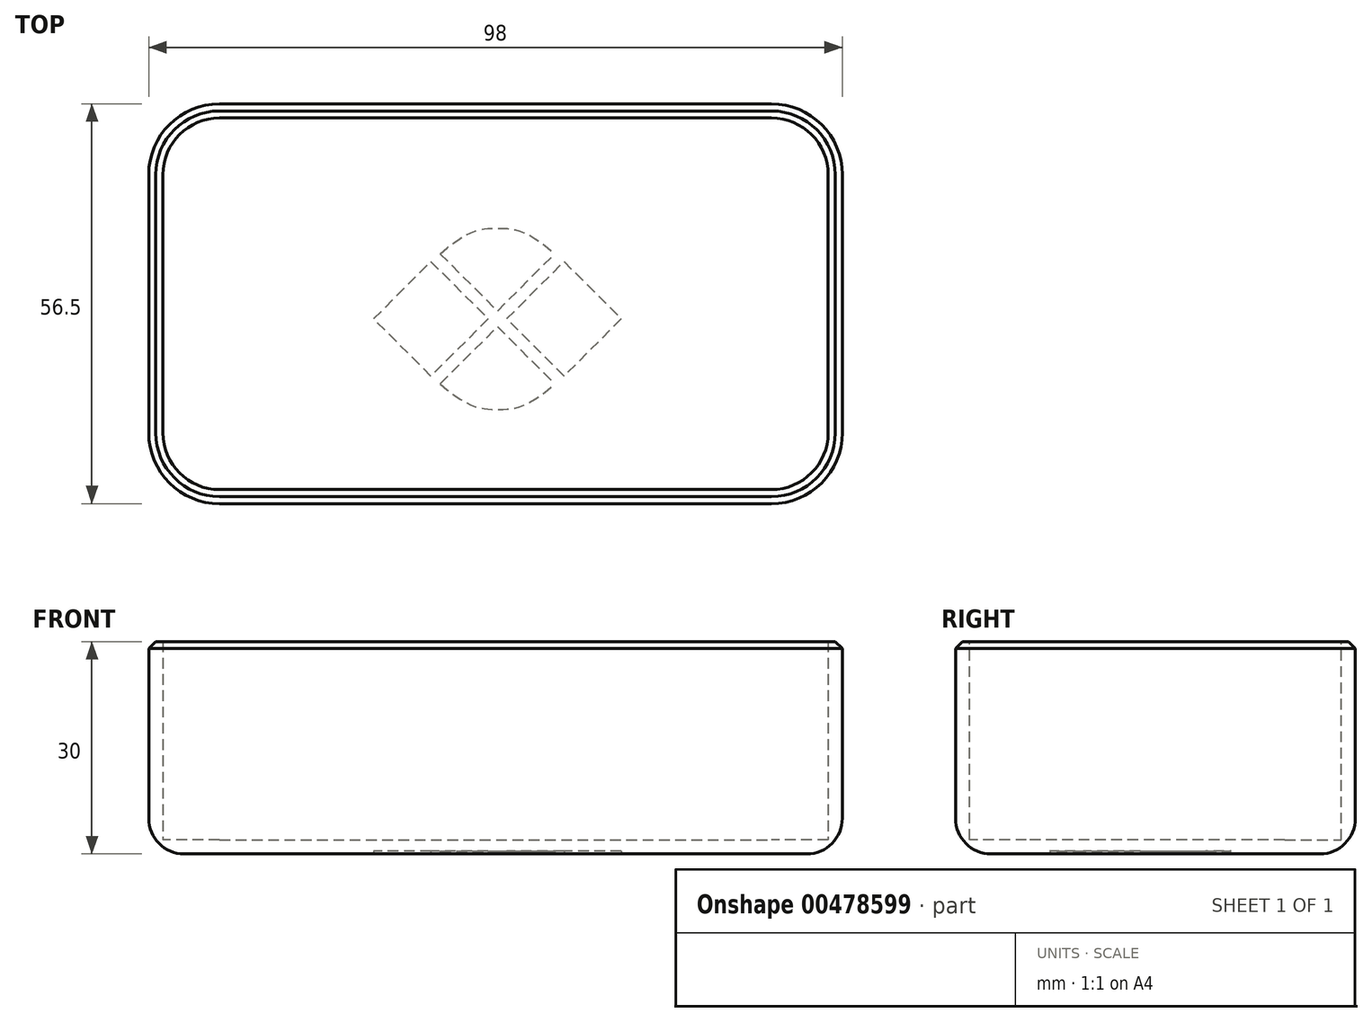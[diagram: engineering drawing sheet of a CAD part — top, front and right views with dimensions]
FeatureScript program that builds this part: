
annotation { "Feature Type Name" : "Feature", "Feature Type Description" : "" }
export const myFeature = defineFeature(function(context is Context, id is Id, definition is map)
    precondition{}
    {
        {
            var Q0;
            Q0=qCreatedBy(makeId("Top.planeOp"),FACE);
            var sketch = newSketch(context, id + "F0", { "sketchPlane" : qUnion([Q0])});
            skLineSegment(sketch, "E0.bottom", {"start": v(-39.28, 30.38) * mm, "end": v(38.72, 30.38) * mm});
            skLineSegment(sketch, "E0.top", {"start": v(-39.28, -26.12) * mm, "end": v(38.72, -26.12) * mm});
            skLineSegment(sketch, "E0.left", {"start": v(-49.28, 20.38) * mm, "end": v(-49.28, -16.12) * mm});
            skLineSegment(sketch, "E0.right", {"start": v(48.72, 20.38) * mm, "end": v(48.72, -16.13) * mm});
            skPoint(sketch, "E1.visualSharp", {"position": v(-49.28, 30.38) * mm});
            skArc(sketch, "E1.filletArc", {"start": v(-39.28, 30.38) * mm, "mid": v(-46.35, 27.45) * mm, "end": v(-49.28, 20.38) * mm});
            skPoint(sketch, "E2.visualSharp", {"position": v(48.72, 30.38) * mm});
            skArc(sketch, "E2.filletArc", {"start": v(48.72, 20.38) * mm, "mid": v(45.8, 27.45) * mm, "end": v(38.72, 30.38) * mm});
            skPoint(sketch, "E3.visualSharp", {"position": v(48.72, -26.12) * mm});
            skArc(sketch, "E3.filletArc", {"start": v(38.72, -26.13) * mm, "mid": v(45.8, -23.2) * mm, "end": v(48.72, -16.13) * mm});
            skPoint(sketch, "E4.visualSharp", {"position": v(-49.28, -26.13) * mm});
            skArc(sketch, "E4.filletArc", {"start": v(-49.28, -16.12) * mm, "mid": v(-46.35, -23.2) * mm, "end": v(-39.28, -26.13) * mm});
            skSolve(sketch);
        }
        {
            var Q0;
            Q0=makeQuery(id+"F0.imprint","IMPRINT",FACE,{"disambiguationData":[TD([[makeQuery(id+"F0.imprint","IMPRINT",EDGE,{"derivedFrom":sQuery(id+"F0.wireOp",EDGE,"E0.bottom")}),-1.0]])]});
            extrude(context, id + "F1", {"entities" : qUnion([Q0]), "depth" : 30 * mm});
        }
        {
            var Q0;
            Q0=makeQuery(id+"F1.opExtrude","CAP_FACE",FACE,{"disambiguationData":[OSD([sQuery(id+"F0.wireOp",EDGE,"E0.bottom"),sQuery(id+"F0.wireOp",EDGE,"E0.top"),sQuery(id+"F0.wireOp",EDGE,"E0.left"),sQuery(id+"F0.wireOp",EDGE,"E0.right"),sQuery(id+"F0.wireOp",EDGE,"E1.filletArc"),sQuery(id+"F0.wireOp",EDGE,"E2.filletArc"),sQuery(id+"F0.wireOp",EDGE,"E3.filletArc"),sQuery(id+"F0.wireOp",EDGE,"E4.filletArc")])],"isStart":false});
            shell(context, id + "F2", {"entities" : qUnion([Q0]), "thickness" : (2) * mm});
        }
        {
            var Q0;
            Q0=makeQuery(id+"F1.opExtrude","CAP_EDGE",EDGE,{"disambiguationData":[OSD([sQuery(id+"F0.wireOp",EDGE,"E0.top")])],"isStart":true});
            fillet(context, id + "F3", {"entities" : qUnion([Q0]), "radius" : 5 * mm, "tangentPropagation" : true, "allowEdgeOverflow" : false});
        }
        {
            var Q0;
            Q0=makeQuery(id+"F1.opExtrude","CAP_EDGE",EDGE,{"disambiguationData":[OSD([sQuery(id+"F0.wireOp",EDGE,"E0.top")])],"isStart":false});
            var Q1;
            Q1=makeQuery(id+"F1.opExtrude","CAP_EDGE",EDGE,{"disambiguationData":[OSD([sQuery(id+"F0.wireOp",EDGE,"E4.filletArc")])],"isStart":false});
            var Q2;
            Q2=makeQuery(id+"F1.opExtrude","CAP_EDGE",EDGE,{"disambiguationData":[OSD([sQuery(id+"F0.wireOp",EDGE,"E0.left")])],"isStart":false});
            var Q3;
            Q3=makeQuery(id+"F1.opExtrude","CAP_EDGE",EDGE,{"disambiguationData":[OSD([sQuery(id+"F0.wireOp",EDGE,"E1.filletArc")])],"isStart":false});
            var Q4;
            Q4=makeQuery(id+"F1.opExtrude","CAP_EDGE",EDGE,{"disambiguationData":[OSD([sQuery(id+"F0.wireOp",EDGE,"E0.bottom")])],"isStart":false});
            var Q5;
            Q5=makeQuery(id+"F1.opExtrude","CAP_EDGE",EDGE,{"disambiguationData":[OSD([sQuery(id+"F0.wireOp",EDGE,"E2.filletArc")])],"isStart":false});
            var Q6;
            Q6=makeQuery(id+"F1.opExtrude","CAP_EDGE",EDGE,{"disambiguationData":[OSD([sQuery(id+"F0.wireOp",EDGE,"E0.right")])],"isStart":false});
            var Q7;
            Q7=makeQuery(id+"F1.opExtrude","CAP_EDGE",EDGE,{"disambiguationData":[OSD([sQuery(id+"F0.wireOp",EDGE,"E3.filletArc")])],"isStart":false});
            chamfer(context, id + "F4", {"entities" : qUnion([Q0, Q1, Q2, Q3, Q4, Q5, Q6, Q7]), "width" : 1 * mm, "tangentPropagation" : true});
        }
        {
            var Q0;
            Q0=makeQuery(id+"F1.opExtrude","CAP_FACE",FACE,{"disambiguationData":[OSD([sQuery(id+"F0.wireOp",EDGE,"E0.bottom"),sQuery(id+"F0.wireOp",EDGE,"E0.top"),sQuery(id+"F0.wireOp",EDGE,"E0.left"),sQuery(id+"F0.wireOp",EDGE,"E0.right"),sQuery(id+"F0.wireOp",EDGE,"E1.filletArc"),sQuery(id+"F0.wireOp",EDGE,"E2.filletArc"),sQuery(id+"F0.wireOp",EDGE,"E3.filletArc"),sQuery(id+"F0.wireOp",EDGE,"E4.filletArc")])],"isStart":true});
            var sketch = newSketch(context, id + "F5", { "sketchPlane" : qUnion([Q0])});
            skLineSegment(sketch, "E5", {"start": v(-8.1, 9.2) * mm, "end": v(0, 1.1) * mm});
            skLineSegment(sketch, "E6", {"start": v(0, 1.1) * mm, "end": v(8.1, 9.2) * mm});
            skLineSegment(sketch, "E7", {"start": v(-9.4, 8.1) * mm, "end": v(-17.5, 0) * mm});
            skLineSegment(sketch, "E8", {"start": v(-17.5, 0) * mm, "end": v(-9.4, -8.1) * mm});
            skLineSegment(sketch, "E9", {"start": v(-9.4, -8.1) * mm, "end": v(-1.31, 0) * mm});
            skLineSegment(sketch, "E10", {"start": v(-1.31, 0) * mm, "end": v(-9.4, 8.1) * mm});
            skLineSegment(sketch, "E11", {"start": v(9.4, 8.1) * mm, "end": v(1.31, 0) * mm});
            skLineSegment(sketch, "E12", {"start": v(1.31, 0) * mm, "end": v(9.4, -8.1) * mm});
            skLineSegment(sketch, "E13", {"start": v(9.4, -8.1) * mm, "end": v(17.5, 0) * mm});
            skLineSegment(sketch, "E14", {"start": v(17.5, 0) * mm, "end": v(9.4, 8.1) * mm});
            skLineSegment(sketch, "E15", {"start": v(0, -1.1) * mm, "end": v(-8.1, -9.2) * mm});
            skLineSegment(sketch, "E16", {"start": v(8.1, -9.2) * mm, "end": v(0, -1.1) * mm});
            skFitSpline(sketch, "E17", {"points": [v(-8.1, 9.2) * mm, v(0, 12.81) * mm, v(8.1, 9.2) * mm], "startDerivative": vector(24.28, 21.71) * mm, "endDerivative": vector(24.28, -21.71) * mm});
            skLineSegment(sketch, "E18.MirrorCS", {"start": v(0, -1.1) * mm, "end": v(8.1, -9.2) * mm});
            skLineSegment(sketch, "E19.MirrorCS", {"start": v(-8.1, -9.2) * mm, "end": v(0, -1.1) * mm});
            skFitSpline(sketch, "E20.MirrorCS", {"points": [v(-8.1, -9.2) * mm, v(0, -12.81) * mm, v(8.1, -9.2) * mm], "startDerivative": vector(24.28, -21.71) * mm, "endDerivative": vector(24.28, 21.71) * mm});
            skSolve(sketch);
        }
        {
            var Q0;
            Q0 = qSketchRegion(id + "F5", true);
            extrude(context, id + "F6", {"entities" : qUnion([Q0]), "operationType" : NewBodyOperationType.REMOVE, "oppositeDirection" : true, "depth" : 0.4 * mm});
        }
    });
